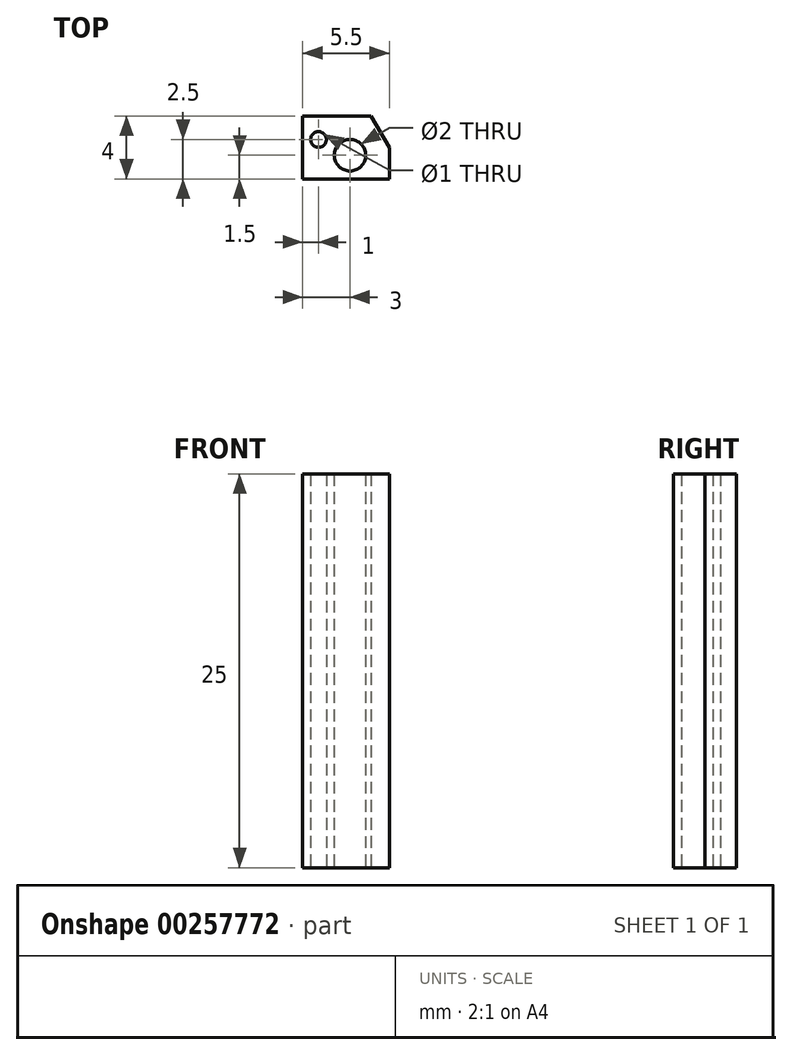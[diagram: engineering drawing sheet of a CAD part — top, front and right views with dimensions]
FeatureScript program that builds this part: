
annotation { "Feature Type Name" : "Feature", "Feature Type Description" : "" }
export const myFeature = defineFeature(function(context is Context, id is Id, definition is map)
    precondition{}
    {
        {
            var Q0;
            Q0=qCreatedBy(makeId("Top.planeOp"),FACE);
            var sketch = newSketch(context, id + "F0", { "sketchPlane" : qUnion([Q0])});
            skLineSegment(sketch, "E0", {"start": v(-13.5, -30.53) * mm, "end": v(-8, -30.53) * mm});
            skLineSegment(sketch, "E1", {"start": v(-8, -30.53) * mm, "end": v(-8, -28.53) * mm});
            skLineSegment(sketch, "E2", {"start": v(-8, -28.53) * mm, "end": v(-9.15, -26.53) * mm});
            skLineSegment(sketch, "E3", {"start": v(-9.15, -26.53) * mm, "end": v(-13.5, -26.53) * mm});
            skLineSegment(sketch, "E4", {"start": v(-13.5, -26.53) * mm, "end": v(-13.5, -30.53) * mm});
            skCircle(sketch, "E5", {"center": v(-10.5, -29.03) * mm, "radius": 0.5 * mm});
            skCircle(sketch, "E6", {"center": v(-10.5, -29.03) * mm, "radius": 1 * mm});
            skCircle(sketch, "E7", {"center": v(-12.5, -28.03) * mm, "radius": 0.5 * mm});
            skSolve(sketch);
        }
        {
            var Q0;
            Q0=makeQuery(id+"F0.imprint","IMPRINT",FACE,{"disambiguationData":[TD([[makeQuery(id+"F0.imprint","IMPRINT",EDGE,{"derivedFrom":sQuery(id+"F0.wireOp",EDGE,"E0")}),1.0]])]});
            extrude(context, id + "F1", {"entities" : qUnion([Q0]), "depth" : 25 * mm});
        }
    });
